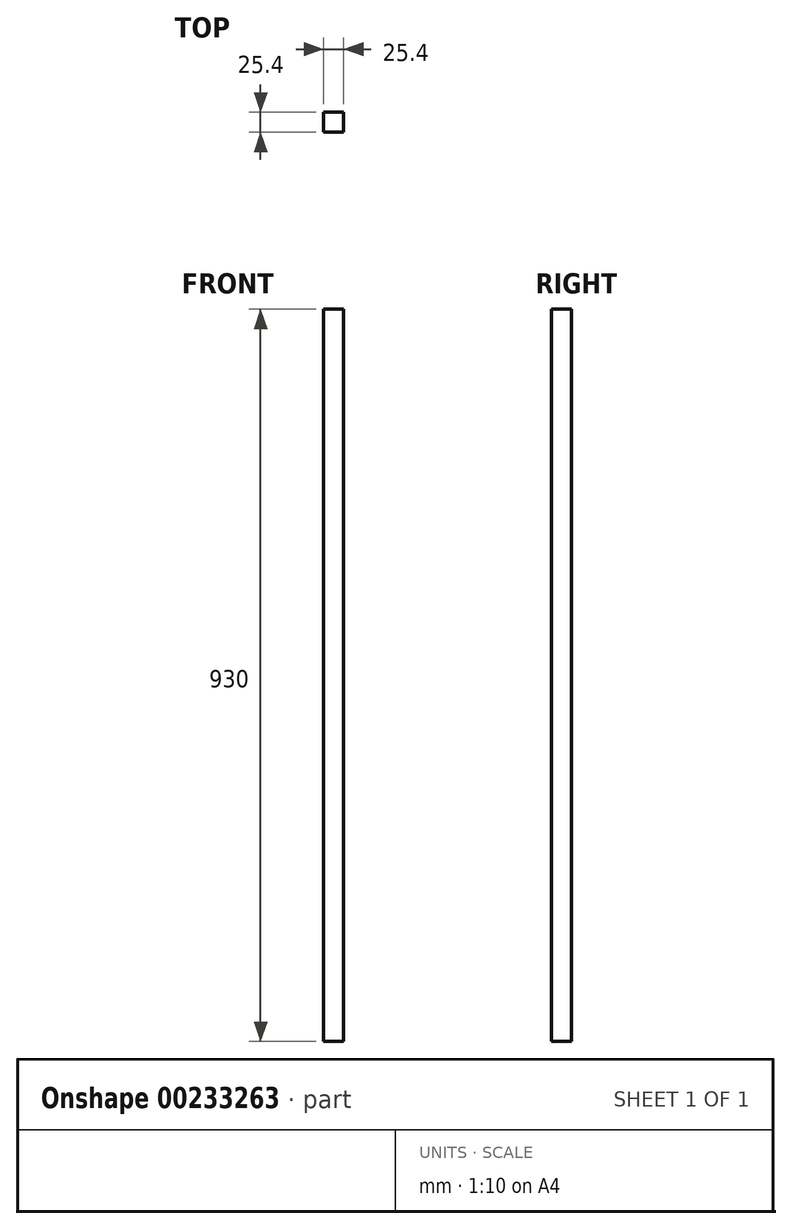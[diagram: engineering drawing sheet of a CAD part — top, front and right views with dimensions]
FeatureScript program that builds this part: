
annotation { "Feature Type Name" : "Feature", "Feature Type Description" : "" }
export const myFeature = defineFeature(function(context is Context, id is Id, definition is map)
    precondition{}
    {
        {
            var Q0;
            Q0=qCreatedBy(makeId("Top.planeOp"),FACE);
            var sketch = newSketch(context, id + "F0", { "sketchPlane" : qUnion([Q0])});
            skLineSegment(sketch, "E0.bottom", {"start": v(-30.41, 46.98) * mm, "end": v(-5.01, 46.98) * mm});
            skLineSegment(sketch, "E0.top", {"start": v(-30.41, 21.58) * mm, "end": v(-5.01, 21.58) * mm});
            skLineSegment(sketch, "E0.left", {"start": v(-30.41, 46.98) * mm, "end": v(-30.41, 21.58) * mm});
            skLineSegment(sketch, "E0.right", {"start": v(-5.01, 46.98) * mm, "end": v(-5.01, 21.58) * mm});
            skSolve(sketch);
        }
        {
            var Q0;
            Q0 = qSketchRegion(id + "F0", true);
            extrude(context, id + "F1", {"entities" : qUnion([Q0]), "depth" : 930 * mm});
        }
    });
